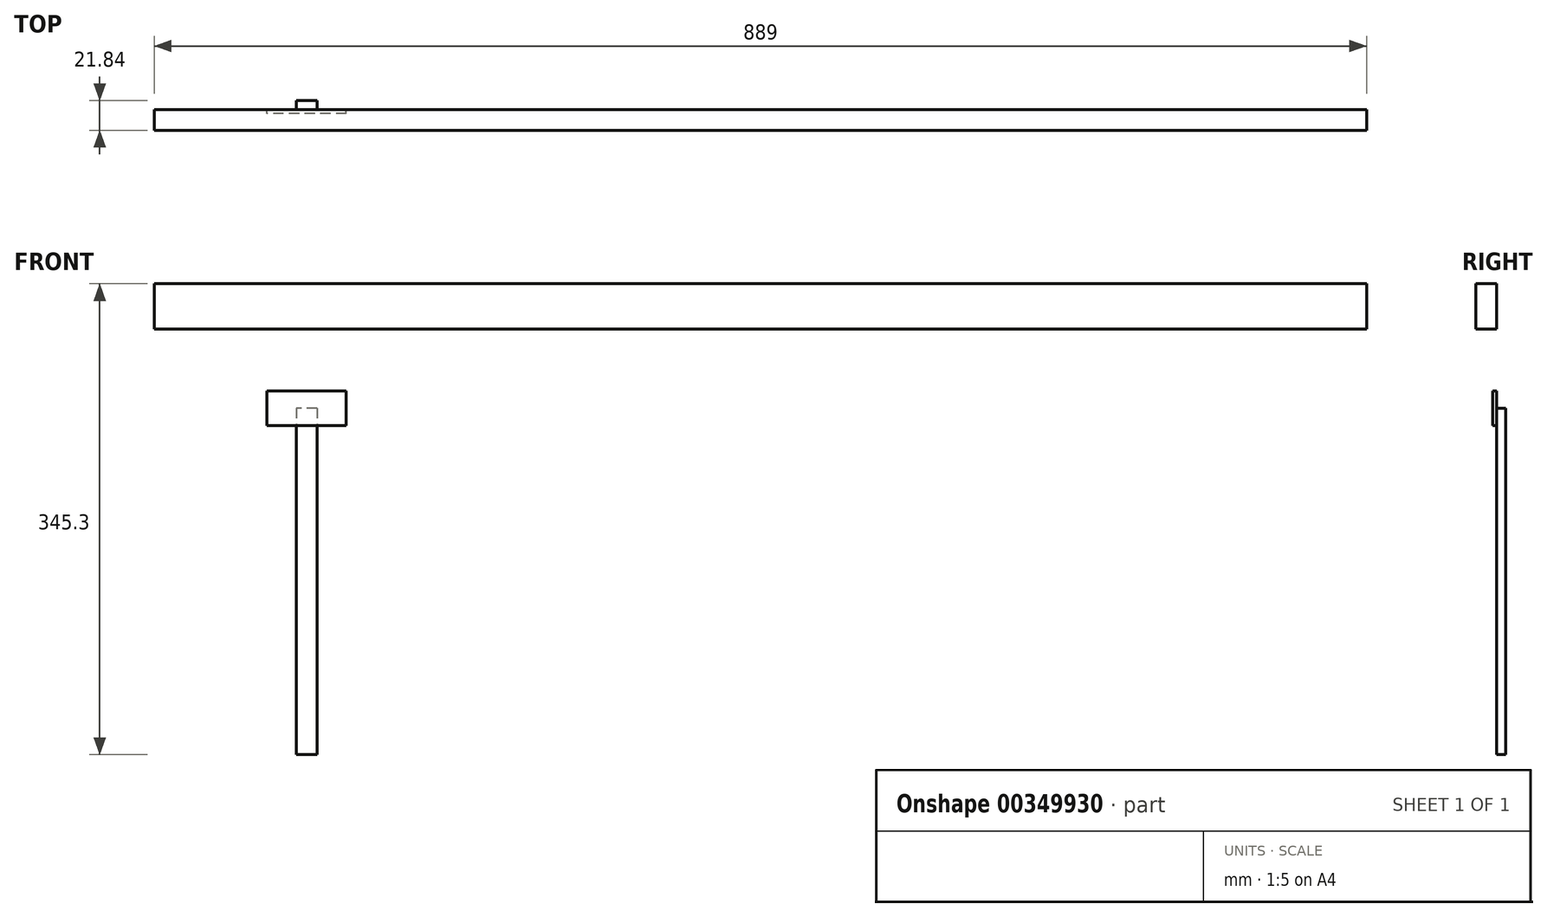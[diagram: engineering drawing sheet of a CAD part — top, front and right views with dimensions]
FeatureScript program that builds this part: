
annotation { "Feature Type Name" : "Feature", "Feature Type Description" : "" }
export const myFeature = defineFeature(function(context is Context, id is Id, definition is map)
    precondition{}
    {
        {
            var Q0;
            Q0=qCreatedBy(makeId("Front.planeOp"),FACE);
            var sketch = newSketch(context, id + "F0", { "sketchPlane" : qUnion([Q0])});
            skLineSegment(sketch, "E0.bottom", {"start": v(29.03, -12.78) * mm, "end": v(-29.03, -12.78) * mm});
            skLineSegment(sketch, "E0.top", {"start": v(29.03, 12.78) * mm, "end": v(-29.03, 12.78) * mm});
            skLineSegment(sketch, "E0.left", {"start": v(29.03, -12.78) * mm, "end": v(29.03, 12.78) * mm});
            skLineSegment(sketch, "E0.right", {"start": v(-29.03, -12.78) * mm, "end": v(-29.03, 12.78) * mm});
            skPoint(sketch, "E0.middle", {"position": v(0, 0) * mm});
            skSolve(sketch);
        }
        {
            var Q0;
            Q0 = qSketchRegion(id + "F0", true);
            extrude(context, id + "F1", {"entities" : qUnion([Q0]), "depth" : 2.8 * mm, "offsetDistance" : 25.4 * mm});
        }
        {
            var Q0;
            Q0=makeQuery(id+"F1.opExtrude","CAP_FACE",FACE,{"disambiguationData":[OSD([sQuery(id+"F0.wireOp",EDGE,"E0.bottom"),sQuery(id+"F0.wireOp",EDGE,"E0.top"),sQuery(id+"F0.wireOp",EDGE,"E0.left"),sQuery(id+"F0.wireOp",EDGE,"E0.right")])],"isStart":true});
            var sketch = newSketch(context, id + "F2", { "sketchPlane" : qUnion([Q0])});
            skLineSegment(sketch, "E1.bottom", {"start": v(-7.68, 0) * mm, "end": v(7.56, 0) * mm});
            skLineSegment(sketch, "E1.top", {"start": v(-7.68, -254) * mm, "end": v(7.56, -254) * mm});
            skLineSegment(sketch, "E1.left", {"start": v(-7.68, 0) * mm, "end": v(-7.68, -254) * mm});
            skLineSegment(sketch, "E1.right", {"start": v(7.56, 0) * mm, "end": v(7.56, -254) * mm});
            skSolve(sketch);
        }
        {
            var Q0;
            Q0 = qSketchRegion(id + "F2", true);
            extrude(context, id + "F3", {"entities" : qUnion([Q0]), "operationType" : NewBodyOperationType.ADD, "depth" : 6.6 * mm, "offsetDistance" : 25.4 * mm});
        }
        {
            var Q0;
            Q0=qCreatedBy(makeId("Front.planeOp"),FACE);
            var sketch = newSketch(context, id + "F4", { "sketchPlane" : qUnion([Q0])});
            skLineSegment(sketch, "E2.bottom", {"start": v(-111.77, 91.3) * mm, "end": v(777.23, 91.3) * mm});
            skLineSegment(sketch, "E2.top", {"start": v(-111.77, 58.06) * mm, "end": v(777.23, 58.06) * mm});
            skLineSegment(sketch, "E2.left", {"start": v(-111.77, 91.3) * mm, "end": v(-111.77, 58.06) * mm});
            skLineSegment(sketch, "E2.right", {"start": v(777.23, 91.3) * mm, "end": v(777.23, 58.06) * mm});
            skSolve(sketch);
        }
        {
            var Q0;
            Q0 = qSketchRegion(id + "F4", true);
            extrude(context, id + "F5", {"entities" : qUnion([Q0]), "depth" : 15.24 * mm, "offsetDistance" : 25.4 * mm});
        }
    });
